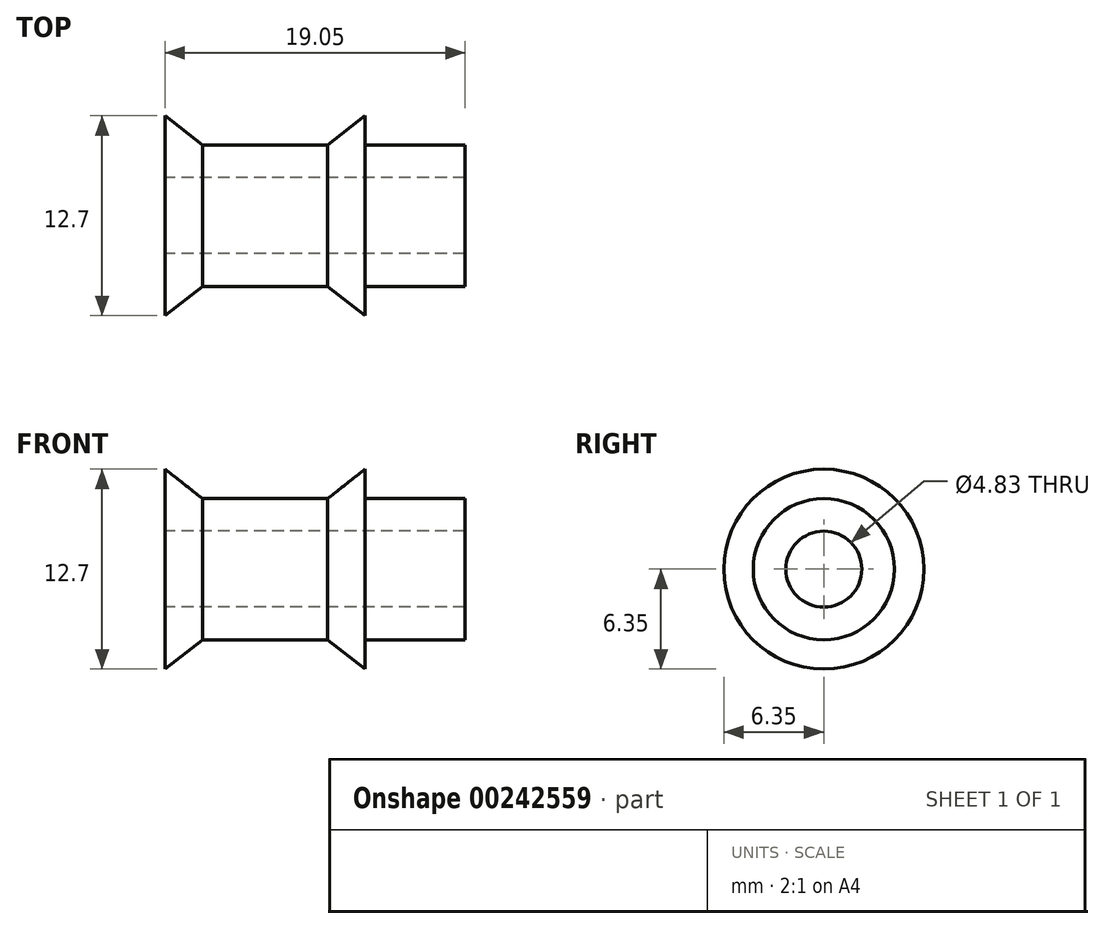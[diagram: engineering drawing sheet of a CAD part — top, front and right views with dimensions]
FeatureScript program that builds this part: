
annotation { "Feature Type Name" : "Feature", "Feature Type Description" : "" }
export const myFeature = defineFeature(function(context is Context, id is Id, definition is map)
    precondition{}
    {
        {
            var Q0;
            Q0=qCreatedBy(makeId("Front.planeOp"),FACE);
            var sketch = newSketch(context, id + "F0", { "sketchPlane" : qUnion([Q0])});
            skLineSegment(sketch, "E0.bottom", {"start": v(-8.38, 4.48) * mm, "end": v(10.67, 4.48) * mm});
            skLineSegment(sketch, "E0.top", {"start": v(-8.38, 2.41) * mm, "end": v(10.67, 2.41) * mm});
            skLineSegment(sketch, "E0.left", {"start": v(-8.38, 4.48) * mm, "end": v(-8.38, 2.41) * mm});
            skLineSegment(sketch, "E0.right", {"start": v(10.67, 4.48) * mm, "end": v(10.67, 2.41) * mm});
            skLineSegment(sketch, "E1.bottom", {"start": v(-8.38, 4.48) * mm, "end": v(-6, 4.48) * mm});
            skLineSegment(sketch, "E1.left", {"start": v(-8.38, 4.48) * mm, "end": v(-8.38, 6.35) * mm});
            skLineSegment(sketch, "E2.bottom", {"start": v(1.94, 4.48) * mm, "end": v(4.32, 4.48) * mm});
            skLineSegment(sketch, "E2.right", {"start": v(4.32, 4.48) * mm, "end": v(4.32, 6.35) * mm});
            skLineSegment(sketch, "E3", {"start": v(-6.08, 0) * mm, "end": v(7.61, 0) * mm});
            skLineSegment(sketch, "E4", {"start": v(-8.38, 6.35) * mm, "end": v(-6, 4.48) * mm});
            skLineSegment(sketch, "E5", {"start": v(1.94, 4.48) * mm, "end": v(4.32, 6.35) * mm});
            skSolve(sketch);
        }
        {
            var Q0;
            Q0 = qSketchRegion(id + "F0", true);
            var Q1;
            Q1=sQuery(id+"F0.wireOp",EDGE,"E3");
            revolve(context, id + "F1", {"entities" : qUnion([Q0]), "axis" : qUnion([Q1]), "revolveType" : RevolveType.FULL});
        }
    });
